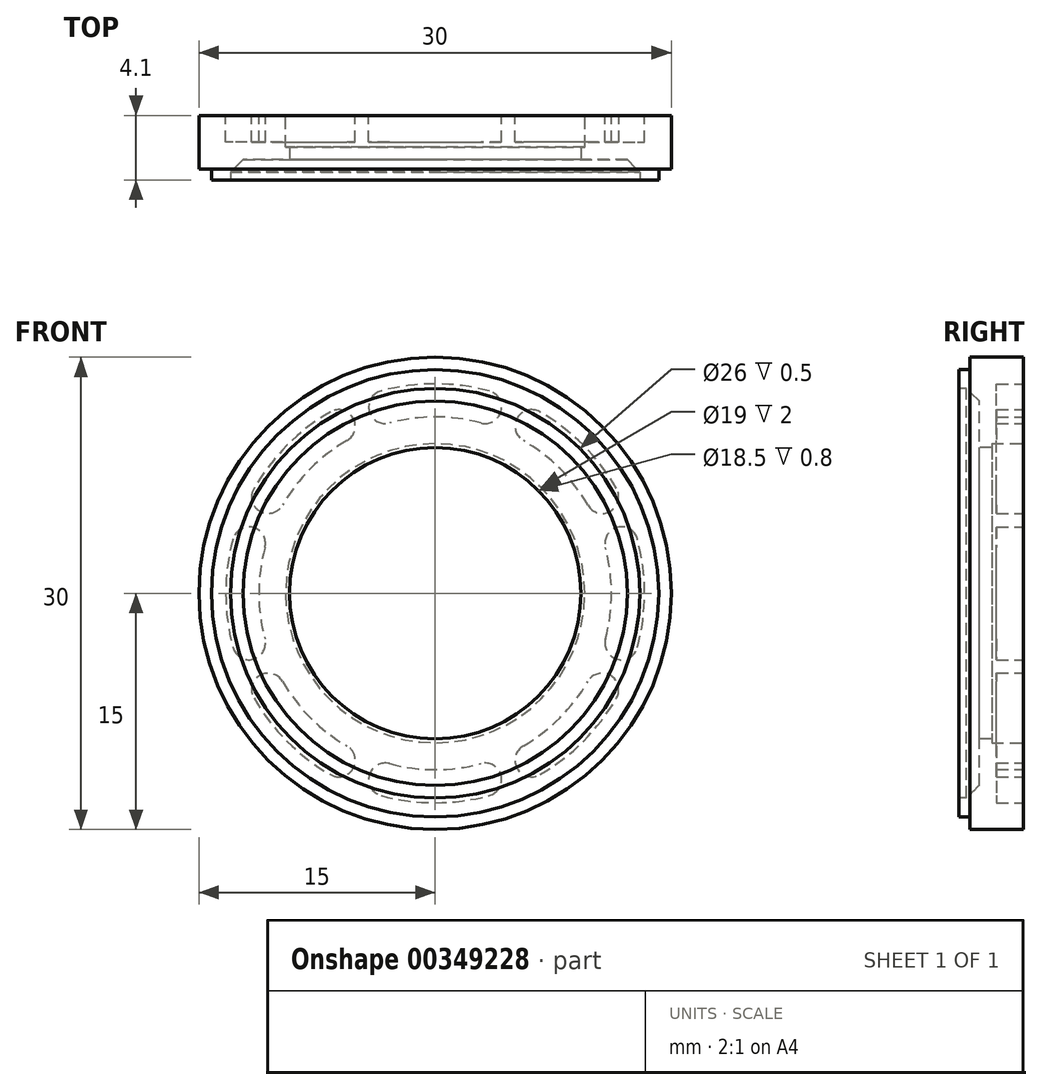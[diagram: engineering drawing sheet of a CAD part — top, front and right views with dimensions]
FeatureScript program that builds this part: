
annotation { "Feature Type Name" : "Feature", "Feature Type Description" : "" }
export const myFeature = defineFeature(function(context is Context, id is Id, definition is map)
    precondition{}
    {
        {
            var Q0;
            Q0=qCreatedBy(makeId("Front.planeOp"),FACE);
            var sketch = newSketch(context, id + "F0", { "sketchPlane" : qUnion([Q0])});
            skCircle(sketch, "E0", {"center": v(0, 0) * mm, "radius": 15 * mm});
            skCircle(sketch, "E1", {"center": v(0, 0) * mm, "radius": 9.5 * mm});
            skCircle(sketch, "E2.1.0", {"center": v(11.83, 3.17) * mm, "radius": 1.05 * mm});
            skCircle(sketch, "E2.2.0", {"center": v(10.6, 6.12) * mm, "radius": 1.05 * mm});
            skCircle(sketch, "E2.4.0", {"center": v(6.13, 10.6) * mm, "radius": 1.05 * mm});
            skCircle(sketch, "E2.5.0", {"center": v(3.17, 11.83) * mm, "radius": 1.05 * mm});
            skCircle(sketch, "E2.7.0", {"center": v(-3.17, 11.83) * mm, "radius": 1.05 * mm});
            skCircle(sketch, "E2.8.0", {"center": v(-6.12, 10.6) * mm, "radius": 1.05 * mm});
            skCircle(sketch, "E2.10.0", {"center": v(-10.6, 6.13) * mm, "radius": 1.05 * mm});
            skCircle(sketch, "E2.11.0", {"center": v(-11.83, 3.17) * mm, "radius": 1.05 * mm});
            skCircle(sketch, "E3", {"center": v(0, 0) * mm, "radius": 11.2 * mm});
            skCircle(sketch, "E4", {"center": v(0, 0) * mm, "radius": 13.3 * mm});
            skCircle(sketch, "E5.1.13.0", {"center": v(-11.83, -3.17) * mm, "radius": 1.05 * mm});
            skCircle(sketch, "E5.1.14.0", {"center": v(-10.6, -6.12) * mm, "radius": 1.05 * mm});
            skCircle(sketch, "E5.1.16.0", {"center": v(-6.13, -10.6) * mm, "radius": 1.05 * mm});
            skCircle(sketch, "E5.1.17.0", {"center": v(-3.17, -11.83) * mm, "radius": 1.05 * mm});
            skCircle(sketch, "E5.1.19.0", {"center": v(3.17, -11.83) * mm, "radius": 1.05 * mm});
            skCircle(sketch, "E5.1.20.0", {"center": v(6.12, -10.6) * mm, "radius": 1.05 * mm});
            skCircle(sketch, "E5.1.22.0", {"center": v(10.6, -6.13) * mm, "radius": 1.05 * mm});
            skCircle(sketch, "E5.1.23.0", {"center": v(11.83, -3.17) * mm, "radius": 1.05 * mm});
            skSolve(sketch);
        }
        {
            var Q0;
            Q0 = qSketchRegion(id + "F0", true);
            var Q1;
            Q1=makeQuery(id+"F0.imprint","IMPRINT",FACE,{"disambiguationData":[TD([[makeQuery(id+"F0.imprint","IMPRINT",EDGE,{"derivedFrom":sQuery(id+"F0.wireOp",EDGE,"E1")}),1.0]])]});
            var Q2;
            {var subQ0=sQuery(id+"F0.wireOp",EDGE,"E3");var subQ1=sQuery(id+"F0.wireOp",EDGE,"vEkXL8x0-xW5C-LHgK-BDgQ-QKywttK1u6fH");var subQ2=makeQuery(id+"F0.imprint","INTERSECT",VERTEX,{"derivedFrom":[subQ1,subQ0]});Q2=makeQuery(id+"F0.imprint","IMPRINT",FACE,{"disambiguationData":[TD([[makeQuery(id+"F0.imprint","IMPRINT",EDGE,{"disambiguationData":[TD([[subQ2,1.0]])],"derivedFrom":subQ1}),-1.0]])]});}
            var Q3;
            {var subQ0=sQuery(id+"F0.wireOp",EDGE,"E3");var subQ1=sQuery(id+"F0.wireOp",EDGE,"E2.10.0");var subQ2=makeQuery(id+"F0.imprint","INTERSECT",VERTEX,{"derivedFrom":[subQ1,subQ0]});Q3=makeQuery(id+"F0.imprint","IMPRINT",FACE,{"disambiguationData":[TD([[makeQuery(id+"F0.imprint","IMPRINT",EDGE,{"disambiguationData":[TD([[subQ2,1.0]])],"derivedFrom":subQ1}),-1.0]])]});}
            var Q4;
            {var subQ0=sQuery(id+"F0.wireOp",EDGE,"E3");var subQ1=sQuery(id+"F0.wireOp",EDGE,"E2.8.0");var subQ2=makeQuery(id+"F0.imprint","INTERSECT",VERTEX,{"derivedFrom":[subQ1,subQ0]});Q4=makeQuery(id+"F0.imprint","IMPRINT",FACE,{"disambiguationData":[TD([[makeQuery(id+"F0.imprint","IMPRINT",EDGE,{"disambiguationData":[TD([[subQ2,1.0]])],"derivedFrom":subQ1}),-1.0]])]});}
            var Q5;
            {var subQ0=sQuery(id+"F0.wireOp",EDGE,"E3");var subQ1=sQuery(id+"F0.wireOp",EDGE,"E2.6.0");var subQ2=makeQuery(id+"F0.imprint","INTERSECT",VERTEX,{"derivedFrom":[subQ1,subQ0]});Q5=makeQuery(id+"F0.imprint","IMPRINT",FACE,{"disambiguationData":[TD([[makeQuery(id+"F0.imprint","IMPRINT",EDGE,{"disambiguationData":[TD([[subQ2,1.0]])],"derivedFrom":subQ1}),-1.0]])]});}
            var Q6;
            {var subQ0=sQuery(id+"F0.wireOp",EDGE,"E3");var subQ1=sQuery(id+"F0.wireOp",EDGE,"E2.4.0");var subQ2=makeQuery(id+"F0.imprint","INTERSECT",VERTEX,{"derivedFrom":[subQ1,subQ0]});Q6=makeQuery(id+"F0.imprint","IMPRINT",FACE,{"disambiguationData":[TD([[makeQuery(id+"F0.imprint","IMPRINT",EDGE,{"disambiguationData":[TD([[subQ2,1.0]])],"derivedFrom":subQ1}),-1.0]])]});}
            var Q7;
            {var subQ0=sQuery(id+"F0.wireOp",EDGE,"E3");var subQ1=sQuery(id+"F0.wireOp",EDGE,"E2.2.0");var subQ2=makeQuery(id+"F0.imprint","INTERSECT",VERTEX,{"derivedFrom":[subQ1,subQ0]});Q7=makeQuery(id+"F0.imprint","IMPRINT",FACE,{"disambiguationData":[TD([[makeQuery(id+"F0.imprint","IMPRINT",EDGE,{"disambiguationData":[TD([[subQ2,1.0]])],"derivedFrom":subQ1}),-1.0]])]});}
            var Q8;
            Q8=makeQuery(id+"F0.imprint","IMPRINT",FACE,{"disambiguationData":[TD([[makeQuery(id+"F0.imprint","IMPRINT",EDGE,{"derivedFrom":sQuery(id+"F0.wireOp",EDGE,"E1")}),-1.0]])]});
            var Q9;
            {var subQ0=sQuery(id+"F0.wireOp",EDGE,"E2.7.0");var subQ1=makeQuery(id+"F0.imprint","INTERSECT",VERTEX,{"derivedFrom":[subQ0,sQuery(id+"F0.wireOp",EDGE,"E3")]});Q9=makeQuery(id+"F0.imprint","IMPRINT",FACE,{"disambiguationData":[TD([[makeQuery(id+"F0.imprint","IMPRINT",EDGE,{"disambiguationData":[TD([[subQ1,1.0]])],"derivedFrom":subQ0}),1.0]])]});}
            var Q10;
            {var subQ0=sQuery(id+"F0.wireOp",EDGE,"E3");var subQ1=sQuery(id+"F0.wireOp",EDGE,"E2.7.0");var subQ2=makeQuery(id+"F0.imprint","INTERSECT",VERTEX,{"derivedFrom":[subQ1,subQ0]});Q10=makeQuery(id+"F0.imprint","IMPRINT",FACE,{"disambiguationData":[TD([[makeQuery(id+"F0.imprint","IMPRINT",EDGE,{"disambiguationData":[TD([[subQ2,1.0]])],"derivedFrom":subQ1}),-1.0]])]});}
            var Q11;
            {var subQ0=sQuery(id+"F0.wireOp",EDGE,"E2.8.0");var subQ1=makeQuery(id+"F0.imprint","INTERSECT",VERTEX,{"derivedFrom":[subQ0,sQuery(id+"F0.wireOp",EDGE,"E3")]});Q11=makeQuery(id+"F0.imprint","IMPRINT",FACE,{"disambiguationData":[TD([[makeQuery(id+"F0.imprint","IMPRINT",EDGE,{"disambiguationData":[TD([[subQ1,1.0]])],"derivedFrom":subQ0}),1.0]])]});}
            var Q12;
            {var subQ0=sQuery(id+"F0.wireOp",EDGE,"E2.9.0");var subQ1=makeQuery(id+"F0.imprint","INTERSECT",VERTEX,{"derivedFrom":[subQ0,sQuery(id+"F0.wireOp",EDGE,"E3")]});Q12=makeQuery(id+"F0.imprint","IMPRINT",FACE,{"disambiguationData":[TD([[makeQuery(id+"F0.imprint","IMPRINT",EDGE,{"disambiguationData":[TD([[subQ1,1.0]])],"derivedFrom":subQ0}),1.0]])]});}
            var Q13;
            {var subQ0=sQuery(id+"F0.wireOp",EDGE,"E3");var subQ1=sQuery(id+"F0.wireOp",EDGE,"E2.9.0");var subQ2=makeQuery(id+"F0.imprint","INTERSECT",VERTEX,{"derivedFrom":[subQ1,subQ0]});Q13=makeQuery(id+"F0.imprint","IMPRINT",FACE,{"disambiguationData":[TD([[makeQuery(id+"F0.imprint","IMPRINT",EDGE,{"disambiguationData":[TD([[subQ2,1.0]])],"derivedFrom":subQ1}),-1.0]])]});}
            var Q14;
            {var subQ0=sQuery(id+"F0.wireOp",EDGE,"E2.10.0");var subQ1=makeQuery(id+"F0.imprint","INTERSECT",VERTEX,{"derivedFrom":[subQ0,sQuery(id+"F0.wireOp",EDGE,"E3")]});Q14=makeQuery(id+"F0.imprint","IMPRINT",FACE,{"disambiguationData":[TD([[makeQuery(id+"F0.imprint","IMPRINT",EDGE,{"disambiguationData":[TD([[subQ1,1.0]])],"derivedFrom":subQ0}),1.0]])]});}
            var Q15;
            {var subQ0=sQuery(id+"F0.wireOp",EDGE,"E2.11.0");var subQ1=makeQuery(id+"F0.imprint","INTERSECT",VERTEX,{"derivedFrom":[subQ0,sQuery(id+"F0.wireOp",EDGE,"E3")]});Q15=makeQuery(id+"F0.imprint","IMPRINT",FACE,{"disambiguationData":[TD([[makeQuery(id+"F0.imprint","IMPRINT",EDGE,{"disambiguationData":[TD([[subQ1,1.0]])],"derivedFrom":subQ0}),1.0]])]});}
            var Q16;
            {var subQ0=sQuery(id+"F0.wireOp",EDGE,"E3");var subQ1=sQuery(id+"F0.wireOp",EDGE,"vEkXL8x0-xW5C-LHgK-BDgQ-QKywttK1u6fH");var subQ2=makeQuery(id+"F0.imprint","INTERSECT",VERTEX,{"derivedFrom":[subQ1,subQ0]});Q16=makeQuery(id+"F0.imprint","IMPRINT",FACE,{"disambiguationData":[TD([[makeQuery(id+"F0.imprint","IMPRINT",EDGE,{"disambiguationData":[TD([[subQ2,-1.0]])],"derivedFrom":subQ1}),-1.0]])]});}
            var Q17;
            {var subQ0=sQuery(id+"F0.wireOp",EDGE,"vEkXL8x0-xW5C-LHgK-BDgQ-QKywttK1u6fH");var subQ1=makeQuery(id+"F0.imprint","INTERSECT",VERTEX,{"derivedFrom":[subQ0,sQuery(id+"F0.wireOp",EDGE,"E3")]});Q17=makeQuery(id+"F0.imprint","IMPRINT",FACE,{"disambiguationData":[TD([[makeQuery(id+"F0.imprint","IMPRINT",EDGE,{"disambiguationData":[TD([[subQ1,1.0]])],"derivedFrom":subQ0}),1.0]])]});}
            var Q18;
            {var subQ0=sQuery(id+"F0.wireOp",EDGE,"E2.1.0");var subQ1=makeQuery(id+"F0.imprint","INTERSECT",VERTEX,{"derivedFrom":[subQ0,sQuery(id+"F0.wireOp",EDGE,"E3")]});Q18=makeQuery(id+"F0.imprint","IMPRINT",FACE,{"disambiguationData":[TD([[makeQuery(id+"F0.imprint","IMPRINT",EDGE,{"disambiguationData":[TD([[subQ1,1.0]])],"derivedFrom":subQ0}),1.0]])]});}
            var Q19;
            {var subQ0=sQuery(id+"F0.wireOp",EDGE,"E3");var subQ1=sQuery(id+"F0.wireOp",EDGE,"E2.1.0");var subQ2=makeQuery(id+"F0.imprint","INTERSECT",VERTEX,{"derivedFrom":[subQ1,subQ0]});Q19=makeQuery(id+"F0.imprint","IMPRINT",FACE,{"disambiguationData":[TD([[makeQuery(id+"F0.imprint","IMPRINT",EDGE,{"disambiguationData":[TD([[subQ2,1.0]])],"derivedFrom":subQ1}),-1.0]])]});}
            var Q20;
            {var subQ0=sQuery(id+"F0.wireOp",EDGE,"E2.2.0");var subQ1=makeQuery(id+"F0.imprint","INTERSECT",VERTEX,{"derivedFrom":[subQ0,sQuery(id+"F0.wireOp",EDGE,"E3")]});Q20=makeQuery(id+"F0.imprint","IMPRINT",FACE,{"disambiguationData":[TD([[makeQuery(id+"F0.imprint","IMPRINT",EDGE,{"disambiguationData":[TD([[subQ1,1.0]])],"derivedFrom":subQ0}),1.0]])]});}
            var Q21;
            {var subQ0=sQuery(id+"F0.wireOp",EDGE,"E2.3.0");var subQ1=makeQuery(id+"F0.imprint","INTERSECT",VERTEX,{"derivedFrom":[subQ0,sQuery(id+"F0.wireOp",EDGE,"E3")]});Q21=makeQuery(id+"F0.imprint","IMPRINT",FACE,{"disambiguationData":[TD([[makeQuery(id+"F0.imprint","IMPRINT",EDGE,{"disambiguationData":[TD([[subQ1,1.0]])],"derivedFrom":subQ0}),1.0]])]});}
            var Q22;
            {var subQ0=sQuery(id+"F0.wireOp",EDGE,"E3");var subQ1=sQuery(id+"F0.wireOp",EDGE,"E2.3.0");var subQ2=makeQuery(id+"F0.imprint","INTERSECT",VERTEX,{"derivedFrom":[subQ1,subQ0]});Q22=makeQuery(id+"F0.imprint","IMPRINT",FACE,{"disambiguationData":[TD([[makeQuery(id+"F0.imprint","IMPRINT",EDGE,{"disambiguationData":[TD([[subQ2,1.0]])],"derivedFrom":subQ1}),-1.0]])]});}
            var Q23;
            {var subQ0=sQuery(id+"F0.wireOp",EDGE,"E2.4.0");var subQ1=makeQuery(id+"F0.imprint","INTERSECT",VERTEX,{"derivedFrom":[subQ0,sQuery(id+"F0.wireOp",EDGE,"E3")]});Q23=makeQuery(id+"F0.imprint","IMPRINT",FACE,{"disambiguationData":[TD([[makeQuery(id+"F0.imprint","IMPRINT",EDGE,{"disambiguationData":[TD([[subQ1,1.0]])],"derivedFrom":subQ0}),1.0]])]});}
            var Q24;
            {var subQ0=sQuery(id+"F0.wireOp",EDGE,"E2.5.0");var subQ1=makeQuery(id+"F0.imprint","INTERSECT",VERTEX,{"derivedFrom":[subQ0,sQuery(id+"F0.wireOp",EDGE,"E3")]});Q24=makeQuery(id+"F0.imprint","IMPRINT",FACE,{"disambiguationData":[TD([[makeQuery(id+"F0.imprint","IMPRINT",EDGE,{"disambiguationData":[TD([[subQ1,1.0]])],"derivedFrom":subQ0}),1.0]])]});}
            var Q25;
            {var subQ0=sQuery(id+"F0.wireOp",EDGE,"E3");var subQ1=sQuery(id+"F0.wireOp",EDGE,"E2.5.0");var subQ2=makeQuery(id+"F0.imprint","INTERSECT",VERTEX,{"derivedFrom":[subQ1,subQ0]});Q25=makeQuery(id+"F0.imprint","IMPRINT",FACE,{"disambiguationData":[TD([[makeQuery(id+"F0.imprint","IMPRINT",EDGE,{"disambiguationData":[TD([[subQ2,1.0]])],"derivedFrom":subQ1}),-1.0]])]});}
            var Q26;
            {var subQ0=sQuery(id+"F0.wireOp",EDGE,"E2.6.0");var subQ1=makeQuery(id+"F0.imprint","INTERSECT",VERTEX,{"derivedFrom":[subQ0,sQuery(id+"F0.wireOp",EDGE,"E3")]});Q26=makeQuery(id+"F0.imprint","IMPRINT",FACE,{"disambiguationData":[TD([[makeQuery(id+"F0.imprint","IMPRINT",EDGE,{"disambiguationData":[TD([[subQ1,1.0]])],"derivedFrom":subQ0}),1.0]])]});}
            var Q27;
            {var subQ0=sQuery(id+"F0.wireOp",EDGE,"E5.1.23.0");var subQ1=makeQuery(id+"F0.imprint","INTERSECT",VERTEX,{"derivedFrom":[sQuery(id+"F0.wireOp",EDGE,"E3"),subQ0]});Q27=makeQuery(id+"F0.imprint","IMPRINT",FACE,{"disambiguationData":[TD([[makeQuery(id+"F0.imprint","IMPRINT",EDGE,{"disambiguationData":[TD([[subQ1,1.0]])],"derivedFrom":subQ0}),1.0]])]});}
            var Q28;
            {var subQ0=sQuery(id+"F0.wireOp",EDGE,"E5.1.22.0");var subQ1=makeQuery(id+"F0.imprint","INTERSECT",VERTEX,{"derivedFrom":[sQuery(id+"F0.wireOp",EDGE,"E3"),subQ0]});Q28=makeQuery(id+"F0.imprint","IMPRINT",FACE,{"disambiguationData":[TD([[makeQuery(id+"F0.imprint","IMPRINT",EDGE,{"disambiguationData":[TD([[subQ1,1.0]])],"derivedFrom":subQ0}),1.0]])]});}
            var Q29;
            {var subQ0=sQuery(id+"F0.wireOp",EDGE,"E5.1.21.0");var subQ1=sQuery(id+"F0.wireOp",EDGE,"E3");var subQ2=makeQuery(id+"F0.imprint","INTERSECT",VERTEX,{"derivedFrom":[subQ1,subQ0]});Q29=makeQuery(id+"F0.imprint","IMPRINT",FACE,{"disambiguationData":[TD([[makeQuery(id+"F0.imprint","IMPRINT",EDGE,{"disambiguationData":[TD([[subQ2,-1.0]])],"derivedFrom":subQ1}),-1.0]])]});}
            var Q30;
            {var subQ0=sQuery(id+"F0.wireOp",EDGE,"E5.1.22.0");var subQ1=sQuery(id+"F0.wireOp",EDGE,"E3");var subQ2=makeQuery(id+"F0.imprint","INTERSECT",VERTEX,{"derivedFrom":[subQ1,subQ0]});Q30=makeQuery(id+"F0.imprint","IMPRINT",FACE,{"disambiguationData":[TD([[makeQuery(id+"F0.imprint","IMPRINT",EDGE,{"disambiguationData":[TD([[subQ2,-1.0]])],"derivedFrom":subQ1}),-1.0]])]});}
            var Q31;
            {var subQ0=sQuery(id+"F0.wireOp",EDGE,"E5.1.21.0");var subQ1=makeQuery(id+"F0.imprint","INTERSECT",VERTEX,{"derivedFrom":[sQuery(id+"F0.wireOp",EDGE,"E3"),subQ0]});Q31=makeQuery(id+"F0.imprint","IMPRINT",FACE,{"disambiguationData":[TD([[makeQuery(id+"F0.imprint","IMPRINT",EDGE,{"disambiguationData":[TD([[subQ1,1.0]])],"derivedFrom":subQ0}),1.0]])]});}
            var Q32;
            {var subQ0=sQuery(id+"F0.wireOp",EDGE,"E5.1.20.0");var subQ1=sQuery(id+"F0.wireOp",EDGE,"E3");var subQ2=makeQuery(id+"F0.imprint","INTERSECT",VERTEX,{"derivedFrom":[subQ1,subQ0]});Q32=makeQuery(id+"F0.imprint","IMPRINT",FACE,{"disambiguationData":[TD([[makeQuery(id+"F0.imprint","IMPRINT",EDGE,{"disambiguationData":[TD([[subQ2,-1.0]])],"derivedFrom":subQ1}),-1.0]])]});}
            var Q33;
            {var subQ0=sQuery(id+"F0.wireOp",EDGE,"E5.1.20.0");var subQ1=makeQuery(id+"F0.imprint","INTERSECT",VERTEX,{"derivedFrom":[sQuery(id+"F0.wireOp",EDGE,"E3"),subQ0]});Q33=makeQuery(id+"F0.imprint","IMPRINT",FACE,{"disambiguationData":[TD([[makeQuery(id+"F0.imprint","IMPRINT",EDGE,{"disambiguationData":[TD([[subQ1,1.0]])],"derivedFrom":subQ0}),1.0]])]});}
            var Q34;
            {var subQ0=sQuery(id+"F0.wireOp",EDGE,"E5.1.19.0");var subQ1=sQuery(id+"F0.wireOp",EDGE,"E3");var subQ2=makeQuery(id+"F0.imprint","INTERSECT",VERTEX,{"derivedFrom":[subQ1,subQ0]});Q34=makeQuery(id+"F0.imprint","IMPRINT",FACE,{"disambiguationData":[TD([[makeQuery(id+"F0.imprint","IMPRINT",EDGE,{"disambiguationData":[TD([[subQ2,-1.0]])],"derivedFrom":subQ1}),-1.0]])]});}
            var Q35;
            {var subQ0=sQuery(id+"F0.wireOp",EDGE,"E5.1.19.0");var subQ1=makeQuery(id+"F0.imprint","INTERSECT",VERTEX,{"derivedFrom":[sQuery(id+"F0.wireOp",EDGE,"E3"),subQ0]});Q35=makeQuery(id+"F0.imprint","IMPRINT",FACE,{"disambiguationData":[TD([[makeQuery(id+"F0.imprint","IMPRINT",EDGE,{"disambiguationData":[TD([[subQ1,1.0]])],"derivedFrom":subQ0}),1.0]])]});}
            var Q36;
            {var subQ0=sQuery(id+"F0.wireOp",EDGE,"E5.1.18.0");var subQ1=sQuery(id+"F0.wireOp",EDGE,"E3");var subQ2=makeQuery(id+"F0.imprint","INTERSECT",VERTEX,{"derivedFrom":[subQ1,subQ0]});Q36=makeQuery(id+"F0.imprint","IMPRINT",FACE,{"disambiguationData":[TD([[makeQuery(id+"F0.imprint","IMPRINT",EDGE,{"disambiguationData":[TD([[subQ2,-1.0]])],"derivedFrom":subQ1}),-1.0]])]});}
            var Q37;
            {var subQ0=sQuery(id+"F0.wireOp",EDGE,"E5.1.18.0");var subQ1=makeQuery(id+"F0.imprint","INTERSECT",VERTEX,{"derivedFrom":[sQuery(id+"F0.wireOp",EDGE,"E3"),subQ0]});Q37=makeQuery(id+"F0.imprint","IMPRINT",FACE,{"disambiguationData":[TD([[makeQuery(id+"F0.imprint","IMPRINT",EDGE,{"disambiguationData":[TD([[subQ1,1.0]])],"derivedFrom":subQ0}),1.0]])]});}
            var Q38;
            {var subQ0=sQuery(id+"F0.wireOp",EDGE,"E5.1.17.0");var subQ1=sQuery(id+"F0.wireOp",EDGE,"E3");var subQ2=makeQuery(id+"F0.imprint","INTERSECT",VERTEX,{"derivedFrom":[subQ1,subQ0]});Q38=makeQuery(id+"F0.imprint","IMPRINT",FACE,{"disambiguationData":[TD([[makeQuery(id+"F0.imprint","IMPRINT",EDGE,{"disambiguationData":[TD([[subQ2,-1.0]])],"derivedFrom":subQ1}),-1.0]])]});}
            var Q39;
            {var subQ0=sQuery(id+"F0.wireOp",EDGE,"E5.1.17.0");var subQ1=makeQuery(id+"F0.imprint","INTERSECT",VERTEX,{"derivedFrom":[sQuery(id+"F0.wireOp",EDGE,"E3"),subQ0]});Q39=makeQuery(id+"F0.imprint","IMPRINT",FACE,{"disambiguationData":[TD([[makeQuery(id+"F0.imprint","IMPRINT",EDGE,{"disambiguationData":[TD([[subQ1,1.0]])],"derivedFrom":subQ0}),1.0]])]});}
            var Q40;
            {var subQ0=sQuery(id+"F0.wireOp",EDGE,"E5.1.16.0");var subQ1=sQuery(id+"F0.wireOp",EDGE,"E3");var subQ2=makeQuery(id+"F0.imprint","INTERSECT",VERTEX,{"derivedFrom":[subQ1,subQ0]});Q40=makeQuery(id+"F0.imprint","IMPRINT",FACE,{"disambiguationData":[TD([[makeQuery(id+"F0.imprint","IMPRINT",EDGE,{"disambiguationData":[TD([[subQ2,-1.0]])],"derivedFrom":subQ1}),-1.0]])]});}
            var Q41;
            {var subQ0=sQuery(id+"F0.wireOp",EDGE,"E5.1.16.0");var subQ1=makeQuery(id+"F0.imprint","INTERSECT",VERTEX,{"derivedFrom":[sQuery(id+"F0.wireOp",EDGE,"E3"),subQ0]});Q41=makeQuery(id+"F0.imprint","IMPRINT",FACE,{"disambiguationData":[TD([[makeQuery(id+"F0.imprint","IMPRINT",EDGE,{"disambiguationData":[TD([[subQ1,1.0]])],"derivedFrom":subQ0}),1.0]])]});}
            var Q42;
            {var subQ0=sQuery(id+"F0.wireOp",EDGE,"E5.1.15.0");var subQ1=sQuery(id+"F0.wireOp",EDGE,"E3");var subQ2=makeQuery(id+"F0.imprint","INTERSECT",VERTEX,{"derivedFrom":[subQ1,subQ0]});Q42=makeQuery(id+"F0.imprint","IMPRINT",FACE,{"disambiguationData":[TD([[makeQuery(id+"F0.imprint","IMPRINT",EDGE,{"disambiguationData":[TD([[subQ2,-1.0]])],"derivedFrom":subQ1}),-1.0]])]});}
            var Q43;
            {var subQ0=sQuery(id+"F0.wireOp",EDGE,"E5.1.15.0");var subQ1=makeQuery(id+"F0.imprint","INTERSECT",VERTEX,{"derivedFrom":[sQuery(id+"F0.wireOp",EDGE,"E3"),subQ0]});Q43=makeQuery(id+"F0.imprint","IMPRINT",FACE,{"disambiguationData":[TD([[makeQuery(id+"F0.imprint","IMPRINT",EDGE,{"disambiguationData":[TD([[subQ1,1.0]])],"derivedFrom":subQ0}),1.0]])]});}
            var Q44;
            {var subQ0=sQuery(id+"F0.wireOp",EDGE,"E5.1.14.0");var subQ1=sQuery(id+"F0.wireOp",EDGE,"E3");var subQ2=makeQuery(id+"F0.imprint","INTERSECT",VERTEX,{"derivedFrom":[subQ1,subQ0]});Q44=makeQuery(id+"F0.imprint","IMPRINT",FACE,{"disambiguationData":[TD([[makeQuery(id+"F0.imprint","IMPRINT",EDGE,{"disambiguationData":[TD([[subQ2,-1.0]])],"derivedFrom":subQ1}),-1.0]])]});}
            var Q45;
            {var subQ0=sQuery(id+"F0.wireOp",EDGE,"E5.1.14.0");var subQ1=makeQuery(id+"F0.imprint","INTERSECT",VERTEX,{"derivedFrom":[sQuery(id+"F0.wireOp",EDGE,"E3"),subQ0]});Q45=makeQuery(id+"F0.imprint","IMPRINT",FACE,{"disambiguationData":[TD([[makeQuery(id+"F0.imprint","IMPRINT",EDGE,{"disambiguationData":[TD([[subQ1,1.0]])],"derivedFrom":subQ0}),1.0]])]});}
            var Q46;
            {var subQ0=sQuery(id+"F0.wireOp",EDGE,"E5.1.13.0");var subQ1=sQuery(id+"F0.wireOp",EDGE,"E3");var subQ2=makeQuery(id+"F0.imprint","INTERSECT",VERTEX,{"derivedFrom":[subQ1,subQ0]});Q46=makeQuery(id+"F0.imprint","IMPRINT",FACE,{"disambiguationData":[TD([[makeQuery(id+"F0.imprint","IMPRINT",EDGE,{"disambiguationData":[TD([[subQ2,-1.0]])],"derivedFrom":subQ1}),-1.0]])]});}
            var Q47;
            {var subQ0=sQuery(id+"F0.wireOp",EDGE,"E5.1.13.0");var subQ1=makeQuery(id+"F0.imprint","INTERSECT",VERTEX,{"derivedFrom":[sQuery(id+"F0.wireOp",EDGE,"E3"),subQ0]});Q47=makeQuery(id+"F0.imprint","IMPRINT",FACE,{"disambiguationData":[TD([[makeQuery(id+"F0.imprint","IMPRINT",EDGE,{"disambiguationData":[TD([[subQ1,1.0]])],"derivedFrom":subQ0}),1.0]])]});}
            var Q48;
            {var subQ0=sQuery(id+"F0.wireOp",EDGE,"E5.1.12.0");var subQ1=sQuery(id+"F0.wireOp",EDGE,"E3");var subQ2=makeQuery(id+"F0.imprint","INTERSECT",VERTEX,{"derivedFrom":[subQ1,subQ0]});Q48=makeQuery(id+"F0.imprint","IMPRINT",FACE,{"disambiguationData":[TD([[makeQuery(id+"F0.imprint","IMPRINT",EDGE,{"disambiguationData":[TD([[subQ2,-1.0]])],"derivedFrom":subQ1}),-1.0]])]});}
            var Q49;
            {var subQ0=sQuery(id+"F0.wireOp",EDGE,"E5.1.12.0");var subQ1=makeQuery(id+"F0.imprint","INTERSECT",VERTEX,{"derivedFrom":[sQuery(id+"F0.wireOp",EDGE,"E3"),subQ0]});Q49=makeQuery(id+"F0.imprint","IMPRINT",FACE,{"disambiguationData":[TD([[makeQuery(id+"F0.imprint","IMPRINT",EDGE,{"disambiguationData":[TD([[subQ1,1.0]])],"derivedFrom":subQ0}),1.0]])]});}
            var Q50;
            {var subQ0=sQuery(id+"F0.wireOp",EDGE,"E3");var subQ1=sQuery(id+"F0.wireOp",EDGE,"E2.11.0");var subQ2=makeQuery(id+"F0.imprint","INTERSECT",VERTEX,{"derivedFrom":[subQ1,subQ0]});Q50=makeQuery(id+"F0.imprint","IMPRINT",FACE,{"disambiguationData":[TD([[makeQuery(id+"F0.imprint","IMPRINT",EDGE,{"disambiguationData":[TD([[subQ2,1.0]])],"derivedFrom":subQ1}),-1.0]])]});}
            extrude(context, id + "F1", {"entities" : qUnion([Q0, Q1, Q2, Q3, Q4, Q5, Q6, Q7, Q8, Q9, Q10, Q11, Q12, Q13, Q14, Q15, Q16, Q17, Q18, Q19, Q20, Q21, Q22, Q23, Q24, Q25, Q26, Q27, Q28, Q29, Q30, Q31, Q32, Q33, Q34, Q35, Q36, Q37, Q38, Q39, Q40, Q41, Q42, Q43, Q44, Q45, Q46, Q47, Q48, Q49, Q50]), "depth" : 4.1 * mm});
        }
        {
            var Q0;
            {var subQ0=sQuery(id+"F0.wireOp",EDGE,"E3");var subQ1=sQuery(id+"F0.wireOp",EDGE,"E2.2.0");var subQ2=makeQuery(id+"F0.imprint","INTERSECT",VERTEX,{"derivedFrom":[subQ1,subQ0]});Q0=makeQuery(id+"F0.imprint","IMPRINT",FACE,{"disambiguationData":[TD([[makeQuery(id+"F0.imprint","IMPRINT",EDGE,{"disambiguationData":[TD([[subQ2,1.0]])],"derivedFrom":subQ1}),-1.0]])]});}
            var Q1;
            {var subQ0=sQuery(id+"F0.wireOp",EDGE,"E2.4.0");var subQ1=makeQuery(id+"F0.imprint","INTERSECT",VERTEX,{"derivedFrom":[subQ0,sQuery(id+"F0.wireOp",EDGE,"E3")]});Q1=makeQuery(id+"F0.imprint","IMPRINT",FACE,{"disambiguationData":[TD([[makeQuery(id+"F0.imprint","IMPRINT",EDGE,{"disambiguationData":[TD([[subQ1,1.0]])],"derivedFrom":subQ0}),1.0]])]});}
            var Q2;
            {var subQ0=sQuery(id+"F0.wireOp",EDGE,"E2.2.0");var subQ1=makeQuery(id+"F0.imprint","INTERSECT",VERTEX,{"derivedFrom":[subQ0,sQuery(id+"F0.wireOp",EDGE,"E3")]});Q2=makeQuery(id+"F0.imprint","IMPRINT",FACE,{"disambiguationData":[TD([[makeQuery(id+"F0.imprint","IMPRINT",EDGE,{"disambiguationData":[TD([[subQ1,1.0]])],"derivedFrom":subQ0}),1.0]])]});}
            var Q3;
            {var subQ0=sQuery(id+"F0.wireOp",EDGE,"E2.5.0");var subQ1=makeQuery(id+"F0.imprint","INTERSECT",VERTEX,{"derivedFrom":[subQ0,sQuery(id+"F0.wireOp",EDGE,"E3")]});Q3=makeQuery(id+"F0.imprint","IMPRINT",FACE,{"disambiguationData":[TD([[makeQuery(id+"F0.imprint","IMPRINT",EDGE,{"disambiguationData":[TD([[subQ1,1.0]])],"derivedFrom":subQ0}),1.0]])]});}
            var Q4;
            {var subQ0=sQuery(id+"F0.wireOp",EDGE,"E3");var subQ1=sQuery(id+"F0.wireOp",EDGE,"E2.5.0");var subQ2=makeQuery(id+"F0.imprint","INTERSECT",VERTEX,{"derivedFrom":[subQ1,subQ0]});Q4=makeQuery(id+"F0.imprint","IMPRINT",FACE,{"disambiguationData":[TD([[makeQuery(id+"F0.imprint","IMPRINT",EDGE,{"disambiguationData":[TD([[subQ2,1.0]])],"derivedFrom":subQ1}),-1.0]])]});}
            var Q5;
            {var subQ0=sQuery(id+"F0.wireOp",EDGE,"E2.7.0");var subQ1=makeQuery(id+"F0.imprint","INTERSECT",VERTEX,{"derivedFrom":[subQ0,sQuery(id+"F0.wireOp",EDGE,"E3")]});Q5=makeQuery(id+"F0.imprint","IMPRINT",FACE,{"disambiguationData":[TD([[makeQuery(id+"F0.imprint","IMPRINT",EDGE,{"disambiguationData":[TD([[subQ1,1.0]])],"derivedFrom":subQ0}),1.0]])]});}
            var Q6;
            {var subQ0=sQuery(id+"F0.wireOp",EDGE,"E2.8.0");var subQ1=makeQuery(id+"F0.imprint","INTERSECT",VERTEX,{"derivedFrom":[subQ0,sQuery(id+"F0.wireOp",EDGE,"E3")]});Q6=makeQuery(id+"F0.imprint","IMPRINT",FACE,{"disambiguationData":[TD([[makeQuery(id+"F0.imprint","IMPRINT",EDGE,{"disambiguationData":[TD([[subQ1,1.0]])],"derivedFrom":subQ0}),1.0]])]});}
            var Q7;
            {var subQ0=sQuery(id+"F0.wireOp",EDGE,"E3");var subQ1=sQuery(id+"F0.wireOp",EDGE,"E2.8.0");var subQ2=makeQuery(id+"F0.imprint","INTERSECT",VERTEX,{"derivedFrom":[subQ1,subQ0]});Q7=makeQuery(id+"F0.imprint","IMPRINT",FACE,{"disambiguationData":[TD([[makeQuery(id+"F0.imprint","IMPRINT",EDGE,{"disambiguationData":[TD([[subQ2,1.0]])],"derivedFrom":subQ1}),-1.0]])]});}
            var Q8;
            {var subQ0=sQuery(id+"F0.wireOp",EDGE,"E2.10.0");var subQ1=makeQuery(id+"F0.imprint","INTERSECT",VERTEX,{"derivedFrom":[subQ0,sQuery(id+"F0.wireOp",EDGE,"E3")]});Q8=makeQuery(id+"F0.imprint","IMPRINT",FACE,{"disambiguationData":[TD([[makeQuery(id+"F0.imprint","IMPRINT",EDGE,{"disambiguationData":[TD([[subQ1,1.0]])],"derivedFrom":subQ0}),1.0]])]});}
            var Q9;
            {var subQ0=sQuery(id+"F0.wireOp",EDGE,"E2.11.0");var subQ1=makeQuery(id+"F0.imprint","INTERSECT",VERTEX,{"derivedFrom":[subQ0,sQuery(id+"F0.wireOp",EDGE,"E3")]});Q9=makeQuery(id+"F0.imprint","IMPRINT",FACE,{"disambiguationData":[TD([[makeQuery(id+"F0.imprint","IMPRINT",EDGE,{"disambiguationData":[TD([[subQ1,1.0]])],"derivedFrom":subQ0}),1.0]])]});}
            var Q10;
            {var subQ0=sQuery(id+"F0.wireOp",EDGE,"E3");var subQ1=sQuery(id+"F0.wireOp",EDGE,"E2.11.0");var subQ2=makeQuery(id+"F0.imprint","INTERSECT",VERTEX,{"derivedFrom":[subQ1,subQ0]});Q10=makeQuery(id+"F0.imprint","IMPRINT",FACE,{"disambiguationData":[TD([[makeQuery(id+"F0.imprint","IMPRINT",EDGE,{"disambiguationData":[TD([[subQ2,1.0]])],"derivedFrom":subQ1}),-1.0]])]});}
            var Q11;
            {var subQ0=sQuery(id+"F0.wireOp",EDGE,"E5.1.13.0");var subQ1=makeQuery(id+"F0.imprint","INTERSECT",VERTEX,{"derivedFrom":[sQuery(id+"F0.wireOp",EDGE,"E3"),subQ0]});Q11=makeQuery(id+"F0.imprint","IMPRINT",FACE,{"disambiguationData":[TD([[makeQuery(id+"F0.imprint","IMPRINT",EDGE,{"disambiguationData":[TD([[subQ1,1.0]])],"derivedFrom":subQ0}),1.0]])]});}
            var Q12;
            {var subQ0=sQuery(id+"F0.wireOp",EDGE,"E5.1.14.0");var subQ1=makeQuery(id+"F0.imprint","INTERSECT",VERTEX,{"derivedFrom":[sQuery(id+"F0.wireOp",EDGE,"E3"),subQ0]});Q12=makeQuery(id+"F0.imprint","IMPRINT",FACE,{"disambiguationData":[TD([[makeQuery(id+"F0.imprint","IMPRINT",EDGE,{"disambiguationData":[TD([[subQ1,1.0]])],"derivedFrom":subQ0}),1.0]])]});}
            var Q13;
            {var subQ0=sQuery(id+"F0.wireOp",EDGE,"E5.1.14.0");var subQ1=sQuery(id+"F0.wireOp",EDGE,"E3");var subQ2=makeQuery(id+"F0.imprint","INTERSECT",VERTEX,{"derivedFrom":[subQ1,subQ0]});Q13=makeQuery(id+"F0.imprint","IMPRINT",FACE,{"disambiguationData":[TD([[makeQuery(id+"F0.imprint","IMPRINT",EDGE,{"disambiguationData":[TD([[subQ2,-1.0]])],"derivedFrom":subQ1}),-1.0]])]});}
            var Q14;
            {var subQ0=sQuery(id+"F0.wireOp",EDGE,"E5.1.16.0");var subQ1=makeQuery(id+"F0.imprint","INTERSECT",VERTEX,{"derivedFrom":[sQuery(id+"F0.wireOp",EDGE,"E3"),subQ0]});Q14=makeQuery(id+"F0.imprint","IMPRINT",FACE,{"disambiguationData":[TD([[makeQuery(id+"F0.imprint","IMPRINT",EDGE,{"disambiguationData":[TD([[subQ1,1.0]])],"derivedFrom":subQ0}),1.0]])]});}
            var Q15;
            {var subQ0=sQuery(id+"F0.wireOp",EDGE,"E5.1.17.0");var subQ1=makeQuery(id+"F0.imprint","INTERSECT",VERTEX,{"derivedFrom":[sQuery(id+"F0.wireOp",EDGE,"E3"),subQ0]});Q15=makeQuery(id+"F0.imprint","IMPRINT",FACE,{"disambiguationData":[TD([[makeQuery(id+"F0.imprint","IMPRINT",EDGE,{"disambiguationData":[TD([[subQ1,1.0]])],"derivedFrom":subQ0}),1.0]])]});}
            var Q16;
            {var subQ0=sQuery(id+"F0.wireOp",EDGE,"E5.1.17.0");var subQ1=sQuery(id+"F0.wireOp",EDGE,"E3");var subQ2=makeQuery(id+"F0.imprint","INTERSECT",VERTEX,{"derivedFrom":[subQ1,subQ0]});Q16=makeQuery(id+"F0.imprint","IMPRINT",FACE,{"disambiguationData":[TD([[makeQuery(id+"F0.imprint","IMPRINT",EDGE,{"disambiguationData":[TD([[subQ2,-1.0]])],"derivedFrom":subQ1}),-1.0]])]});}
            var Q17;
            {var subQ0=sQuery(id+"F0.wireOp",EDGE,"E5.1.19.0");var subQ1=makeQuery(id+"F0.imprint","INTERSECT",VERTEX,{"derivedFrom":[sQuery(id+"F0.wireOp",EDGE,"E3"),subQ0]});Q17=makeQuery(id+"F0.imprint","IMPRINT",FACE,{"disambiguationData":[TD([[makeQuery(id+"F0.imprint","IMPRINT",EDGE,{"disambiguationData":[TD([[subQ1,1.0]])],"derivedFrom":subQ0}),1.0]])]});}
            var Q18;
            {var subQ0=sQuery(id+"F0.wireOp",EDGE,"E5.1.20.0");var subQ1=makeQuery(id+"F0.imprint","INTERSECT",VERTEX,{"derivedFrom":[sQuery(id+"F0.wireOp",EDGE,"E3"),subQ0]});Q18=makeQuery(id+"F0.imprint","IMPRINT",FACE,{"disambiguationData":[TD([[makeQuery(id+"F0.imprint","IMPRINT",EDGE,{"disambiguationData":[TD([[subQ1,1.0]])],"derivedFrom":subQ0}),1.0]])]});}
            var Q19;
            {var subQ0=sQuery(id+"F0.wireOp",EDGE,"E5.1.20.0");var subQ1=sQuery(id+"F0.wireOp",EDGE,"E3");var subQ2=makeQuery(id+"F0.imprint","INTERSECT",VERTEX,{"derivedFrom":[subQ1,subQ0]});Q19=makeQuery(id+"F0.imprint","IMPRINT",FACE,{"disambiguationData":[TD([[makeQuery(id+"F0.imprint","IMPRINT",EDGE,{"disambiguationData":[TD([[subQ2,-1.0]])],"derivedFrom":subQ1}),-1.0]])]});}
            var Q20;
            {var subQ0=sQuery(id+"F0.wireOp",EDGE,"E5.1.22.0");var subQ1=makeQuery(id+"F0.imprint","INTERSECT",VERTEX,{"derivedFrom":[sQuery(id+"F0.wireOp",EDGE,"E3"),subQ0]});Q20=makeQuery(id+"F0.imprint","IMPRINT",FACE,{"disambiguationData":[TD([[makeQuery(id+"F0.imprint","IMPRINT",EDGE,{"disambiguationData":[TD([[subQ1,1.0]])],"derivedFrom":subQ0}),1.0]])]});}
            var Q21;
            {var subQ0=sQuery(id+"F0.wireOp",EDGE,"E5.1.23.0");var subQ1=makeQuery(id+"F0.imprint","INTERSECT",VERTEX,{"derivedFrom":[sQuery(id+"F0.wireOp",EDGE,"E3"),subQ0]});Q21=makeQuery(id+"F0.imprint","IMPRINT",FACE,{"disambiguationData":[TD([[makeQuery(id+"F0.imprint","IMPRINT",EDGE,{"disambiguationData":[TD([[subQ1,1.0]])],"derivedFrom":subQ0}),1.0]])]});}
            var Q22;
            {var subQ0=sQuery(id+"F0.wireOp",EDGE,"E2.1.0");var subQ1=makeQuery(id+"F0.imprint","INTERSECT",VERTEX,{"derivedFrom":[subQ0,sQuery(id+"F0.wireOp",EDGE,"E3")]});Q22=makeQuery(id+"F0.imprint","IMPRINT",FACE,{"disambiguationData":[TD([[makeQuery(id+"F0.imprint","IMPRINT",EDGE,{"disambiguationData":[TD([[subQ1,1.0]])],"derivedFrom":subQ0}),1.0]])]});}
            var Q23;
            {var subQ0=sQuery(id+"F0.wireOp",EDGE,"E3");var subQ1=sQuery(id+"F0.wireOp",EDGE,"E2.1.0");var subQ2=makeQuery(id+"F0.imprint","INTERSECT",VERTEX,{"derivedFrom":[subQ1,subQ0]});Q23=makeQuery(id+"F0.imprint","IMPRINT",FACE,{"disambiguationData":[TD([[makeQuery(id+"F0.imprint","IMPRINT",EDGE,{"disambiguationData":[TD([[subQ2,-1.0]])],"derivedFrom":subQ1}),-1.0]])]});}
            extrude(context, id + "F2", {"entities" : qUnion([Q0, Q1, Q2, Q3, Q4, Q5, Q6, Q7, Q8, Q9, Q10, Q11, Q12, Q13, Q14, Q15, Q16, Q17, Q18, Q19, Q20, Q21, Q22, Q23]), "operationType" : NewBodyOperationType.REMOVE, "depth" : 1.7 * mm});
        }
        {
            var Q0;
            Q0=makeQuery(id+"F1.opExtrude","CAP_FACE",FACE,{"disambiguationData":[OSD([sQuery(id+"F0.wireOp",EDGE,"E0")])],"isStart":false});
            var sketch = newSketch(context, id + "F3", { "sketchPlane" : qUnion([Q0])});
            skCircle(sketch, "E6", {"center": v(0, 0) * mm, "radius": 13 * mm});
            skCircle(sketch, "E7", {"center": v(0, 0) * mm, "radius": 14.2 * mm});
            skSolve(sketch);
        }
        {
            var Q0;
            Q0=makeQuery(id+"F3.imprint","IMPRINT",FACE,{"disambiguationData":[TD([[makeQuery(id+"F3.imprint","IMPRINT",EDGE,{"derivedFrom":sQuery(id+"F3.wireOp",EDGE,"E7")}),-1.0]])]});
            extrude(context, id + "F4", {"entities" : qUnion([Q0]), "operationType" : NewBodyOperationType.REMOVE, "oppositeDirection" : true, "depth" : 0.7 * mm});
        }
        {
            var Q0;
            Q0=makeQuery(id+"F4.boolean.opBoolean","SPLIT",FACE,{"disambiguationData":[TD([makeQuery(id+"F4.opExtrude","SWEPT_FACE",FACE,{"disambiguationData":[OSD([sQuery(id+"F3.wireOp",EDGE,"E6")])]})])],"derivedFrom":makeQuery(id+"F1.opExtrude","CAP_FACE",FACE,{"disambiguationData":[OSD([sQuery(id+"F0.wireOp",EDGE,"E0")])],"isStart":false})});
            var sketch = newSketch(context, id + "F5", { "sketchPlane" : qUnion([Q0])});
            skCircle(sketch, "E8", {"center": v(0, 0) * mm, "radius": 13 * mm});
            skSolve(sketch);
        }
        {
            var Q0;
            Q0=makeQuery(id+"F5.imprint","IMPRINT",FACE,{"disambiguationData":[TD([[makeQuery(id+"F5.imprint","IMPRINT",EDGE,{"derivedFrom":sQuery(id+"F5.wireOp",EDGE,"E8")}),1.0]])]});
            extrude(context, id + "F6", {"entities" : qUnion([Q0]), "operationType" : NewBodyOperationType.REMOVE, "oppositeDirection" : true, "depth" : 1.3 * mm});
        }
        {
            var Q0;
            Q0=makeQuery(id+"F1.opExtrude","CAP_FACE",FACE,{"disambiguationData":[OSD([sQuery(id+"F0.wireOp",EDGE,"E0")])],"isStart":true});
            var sketch = newSketch(context, id + "F7", { "sketchPlane" : qUnion([Q0])});
            skCircle(sketch, "E9", {"center": v(0, 0) * mm, "radius": 9.5 * mm});
            skSolve(sketch);
        }
        {
            var Q0;
            Q0=makeQuery(id+"F7.imprint","IMPRINT",FACE,{"disambiguationData":[TD([[makeQuery(id+"F7.imprint","IMPRINT",EDGE,{"derivedFrom":sQuery(id+"F7.wireOp",EDGE,"E9")}),1.0]])]});
            extrude(context, id + "F8", {"entities" : qUnion([Q0]), "operationType" : NewBodyOperationType.REMOVE, "oppositeDirection" : true, "depth" : 2 * mm});
        }
        {
            var Q0;
            Q0=makeQuery(id+"F6.boolean.opBoolean","COPY",FACE,{"derivedFrom":makeQuery(id+"F6.opExtrude","CAP_FACE",FACE,{"disambiguationData":[OSD([sQuery(id+"F5.wireOp",EDGE,"E8")])],"isStart":false})});
            chamfer(context, id + "F9", {"entities" : qUnion([Q0]), "width" : .8 * mm, "tangentPropagation" : true});
        }
        {
            var Q0;
            Q0=makeQuery(id+"F6.boolean.opBoolean","COPY",FACE,{"derivedFrom":makeQuery(id+"F6.opExtrude","CAP_FACE",FACE,{"disambiguationData":[OSD([sQuery(id+"F5.wireOp",EDGE,"E8")])],"isStart":false})});
            var sketch = newSketch(context, id + "F10", { "sketchPlane" : qUnion([Q0])});
            skCircle(sketch, "E10", {"center": v(0, 0) * mm, "radius": 9.25 * mm});
            skSolve(sketch);
        }
        {
            var Q0;
            Q0=makeQuery(id+"F10.imprint","IMPRINT",FACE,{"disambiguationData":[TD([[makeQuery(id+"F10.imprint","IMPRINT",EDGE,{"derivedFrom":sQuery(id+"F10.wireOp",EDGE,"E10")}),1.0]])]});
            extrude(context, id + "F11", {"entities" : qUnion([Q0]), "operationType" : NewBodyOperationType.REMOVE, "oppositeDirection" : true, "depth" : 2 * mm});
        }
    });
